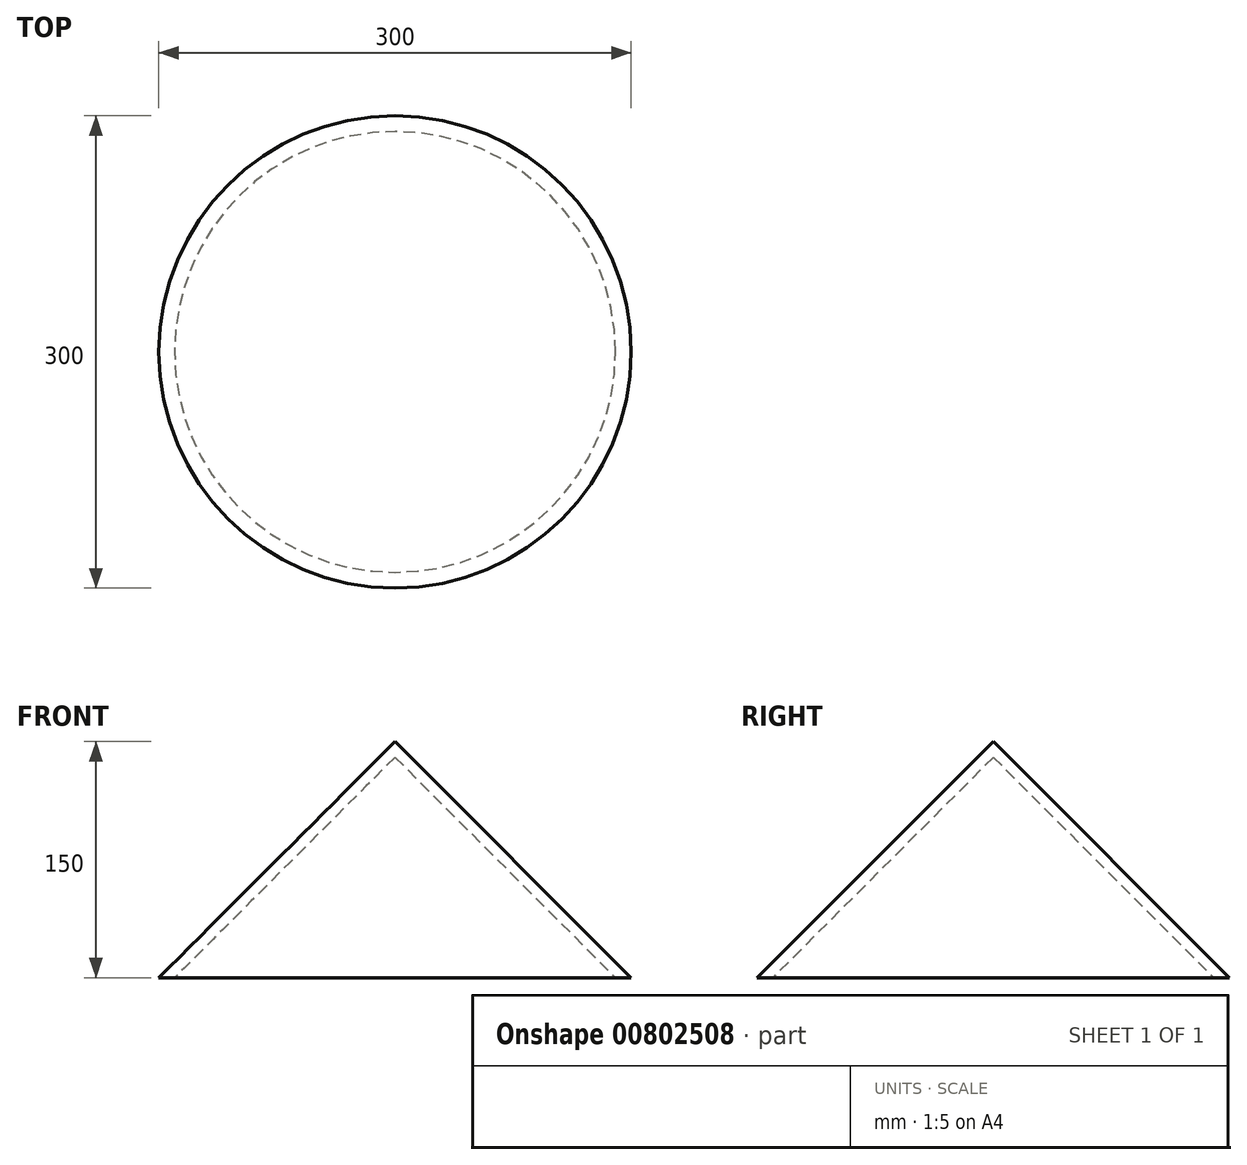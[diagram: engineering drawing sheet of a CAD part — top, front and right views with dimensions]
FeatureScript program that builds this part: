
annotation { "Feature Type Name" : "Feature", "Feature Type Description" : "" }
export const myFeature = defineFeature(function(context is Context, id is Id, definition is map)
    precondition{}
    {
        {
            var Q0;
            Q0=qCreatedBy(makeId("Front.planeOp"),FACE);
            var sketch = newSketch(context, id + "F0", { "sketchPlane" : qUnion([Q0])});
            skLineSegment(sketch, "E0", {"start": v(0, 0) * mm, "end": v(-150, 0) * mm});
            skLineSegment(sketch, "E1", {"start": v(-150, 0) * mm, "end": v(0, 150) * mm});
            skLineSegment(sketch, "E2", {"start": v(0, 0) * mm, "end": v(0, 150) * mm});
            skLineSegment(sketch, "E3", {"start": v(0, 0) * mm, "end": v(-140, 0) * mm});
            skLineSegment(sketch, "E4", {"start": v(0, 0) * mm, "end": v(0, 140) * mm});
            skLineSegment(sketch, "E5", {"start": v(0, 140) * mm, "end": v(-140, 0) * mm});
            skSolve(sketch);
        }
        {
            var Q0;
            {var subQ0=sQuery(id+"F0.wireOp",EDGE,"E1");Q0=makeQuery(id+"F0.imprint","IMPRINT",FACE,{"disambiguationData":[TD([[makeQuery(id+"F0.imprint","IMPRINT",EDGE,{"derivedFrom":subQ0}),-1.0]])]});}
            var Q1;
            Q1=sQuery(id+"F0.wireOp",EDGE,"E4");
            revolve(context, id + "F1", {"surfaceOperationType" : NewSurfaceOperationType.NEW, "entities" : qUnion([Q0]), "axis" : qUnion([Q1]), "revolveType" : RevolveType.FULL});
        }
    });
